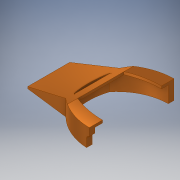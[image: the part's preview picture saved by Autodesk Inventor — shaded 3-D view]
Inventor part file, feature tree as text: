
AUTODESK INVENTOR PART (.ipt)
format: ipt  version: 2019 (Build 230136000, 136)  size: 1,518,080 bytes
history: native  units: mm
features: sketch x8, other x7, extrude x5, projected_geometry x5, plane x4, revolve x2, fillet x1
ambient origin geometry x8: Origin, YZ Plane, XZ Plane, XY Plane, X Axis, Y Axis, Z Axis, Center Point
bodies: Volumenkörper1 (feature_tree)
feature tree (32):
  sketch  "Skizze1"  dims[d9=15.2mm d12=13.036764mm]
  sketch  "Skizze2"  dims[d38=15.2mm d47=8.714705mm]
  sketch  "Skizze3"  dims[d49=8.715mm d57=15.197209mm]
  extrude  "Extrusion1"  Depth=13.036764mm
  extrude  "Extrusion3"  Depth=8.714705mm
  extrude  "Extrusion4"  Depth=15.197209mm
  extrude  "Extrusion5"  Depth=11.912488mm
  plane  "Arbeitsebene4"
  other  "Trennen4"
  plane  "Arbeitsebene5"
  plane  "Arbeitsebene6"
  other  "Trennen5"
  plane  "Arbeitsebene3"
  other  "Trennen3"
  fillet  "Rundung5"  Radius=1.077mm
  extrude  "Extrusion6"  Depth=8.853mm
  revolve  "Umdrehung2"
  revolve  "Umdrehung3"
  other  "Bild2"
  other  "Bild3"
  other  "Bild4"
  sketch  "Skizze8"  dims[d58=15.197209mm d59=11.912488mm d60=1.077mm]
  projected_geometry  "Projizierte Kontur4"
  sketch  "Skizze9"  dims[d61=3.1mm d62=0.0mm d67=8.853mm]
  projected_geometry  "Projizierte Kontur5"
  sketch  "Skizze10"  dims[d69=0.0mm]
  projected_geometry  "Projizierte Kontur6"
  projected_geometry  "Projizierte Kontur7"
  sketch  "Skizze12"  dims[d70=8.853mm]
  projected_geometry  "Projizierte Kontur8"
  sketch  "Skizze13"  dims[d73=0.5mm d74=0.0mm d75=0.6mm d76=90.0deg d77=1.55mm d78=0.5mm d79=0.0mm d80=5.0mm d82=8.798192mm d84=4.0mm d85=4.0mm d86=4.8mm d87=0.0mm d91=1.745329mm d92=1.0mm d95=2.3mm d96=0.0mm d98=-2.268928mm d102=1.0mm d103=1.745329mm d104=1.0mm d105=1.0mm d112=10.07mm d116=9.964mm d117=-3.141593mm]
  other  "Arbeitsachse4"
